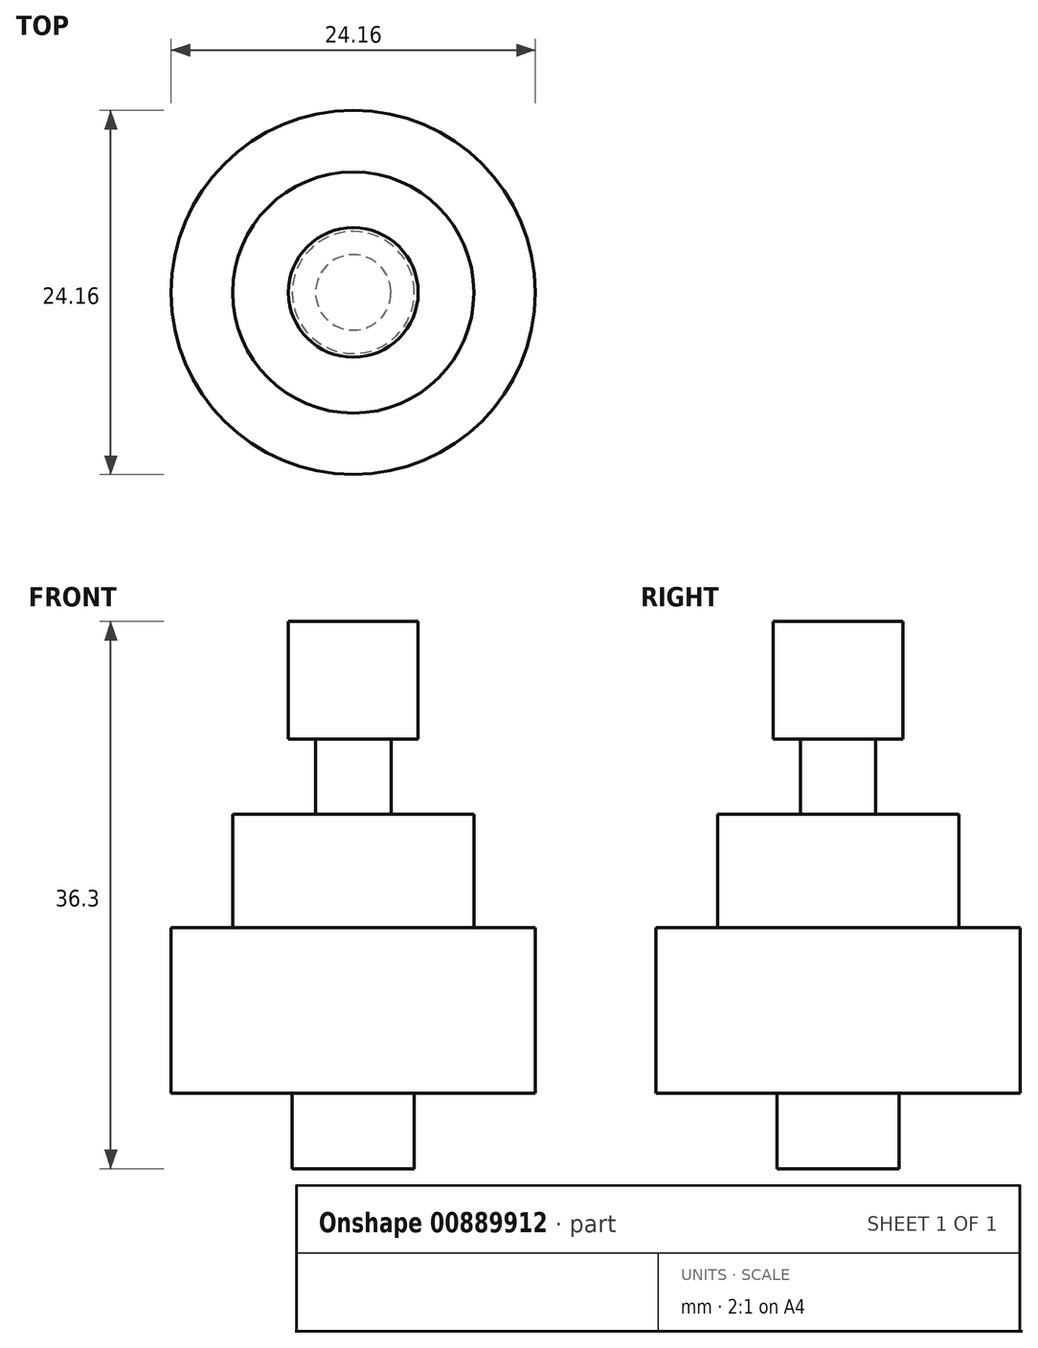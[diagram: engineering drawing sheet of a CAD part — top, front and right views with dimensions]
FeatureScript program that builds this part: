
annotation { "Feature Type Name" : "Feature", "Feature Type Description" : "" }
export const myFeature = defineFeature(function(context is Context, id is Id, definition is map)
    precondition{}
    {
        {
            var Q0;
            Q0=qCreatedBy(makeId("Front.planeOp"),FACE);
            var sketch = newSketch(context, id + "F0", { "sketchPlane" : qUnion([Q0])});
            skLineSegment(sketch, "E0", {"start": v(0, 37.38) * mm, "end": v(0, -31.69) * mm, "construction": true});
            skLineSegment(sketch, "E1", {"start": v(0, 0) * mm, "end": v(-4.05, 0) * mm});
            skLineSegment(sketch, "E2", {"start": v(-4.05, 0) * mm, "end": v(-4.05, 5) * mm});
            skLineSegment(sketch, "E3", {"start": v(-4.05, 5) * mm, "end": v(-12.08, 5) * mm});
            skLineSegment(sketch, "E4", {"start": v(-12.08, 5) * mm, "end": v(-12.08, 16) * mm});
            skLineSegment(sketch, "E5", {"start": v(-12.08, 16) * mm, "end": v(-8, 16) * mm});
            skLineSegment(sketch, "E6", {"start": v(-8, 16) * mm, "end": v(-8, 23.5) * mm});
            skLineSegment(sketch, "E7", {"start": v(-8, 23.5) * mm, "end": v(-2.5, 23.5) * mm});
            skLineSegment(sketch, "E8", {"start": v(-2.5, 23.5) * mm, "end": v(-2.5, 28.5) * mm});
            skLineSegment(sketch, "E9", {"start": v(-2.5, 28.5) * mm, "end": v(-4.3, 28.5) * mm});
            skLineSegment(sketch, "E10", {"start": v(-4.3, 28.5) * mm, "end": v(-4.3, 36.3) * mm});
            skLineSegment(sketch, "E11", {"start": v(-4.3, 36.3) * mm, "end": v(0, 36.3) * mm});
            skLineSegment(sketch, "E12", {"start": v(0, 36.3) * mm, "end": v(0, 0) * mm});
            skSolve(sketch);
        }
        {
            var Q0;
            Q0=makeQuery(id+"F0.imprint","IMPRINT",FACE,{"disambiguationData":[TD([[makeQuery(id+"F0.imprint","IMPRINT",EDGE,{"derivedFrom":sQuery(id+"F0.wireOp",EDGE,"E1")}),-1.0]])]});
            var Q1;
            Q1=sQuery(id+"F0.wireOp",EDGE,"E12");
            revolve(context, id + "F1", {"surfaceOperationType" : NewSurfaceOperationType.NEW, "entities" : qUnion([Q0]), "axis" : qUnion([Q1]), "revolveType" : RevolveType.FULL});
        }
    });
